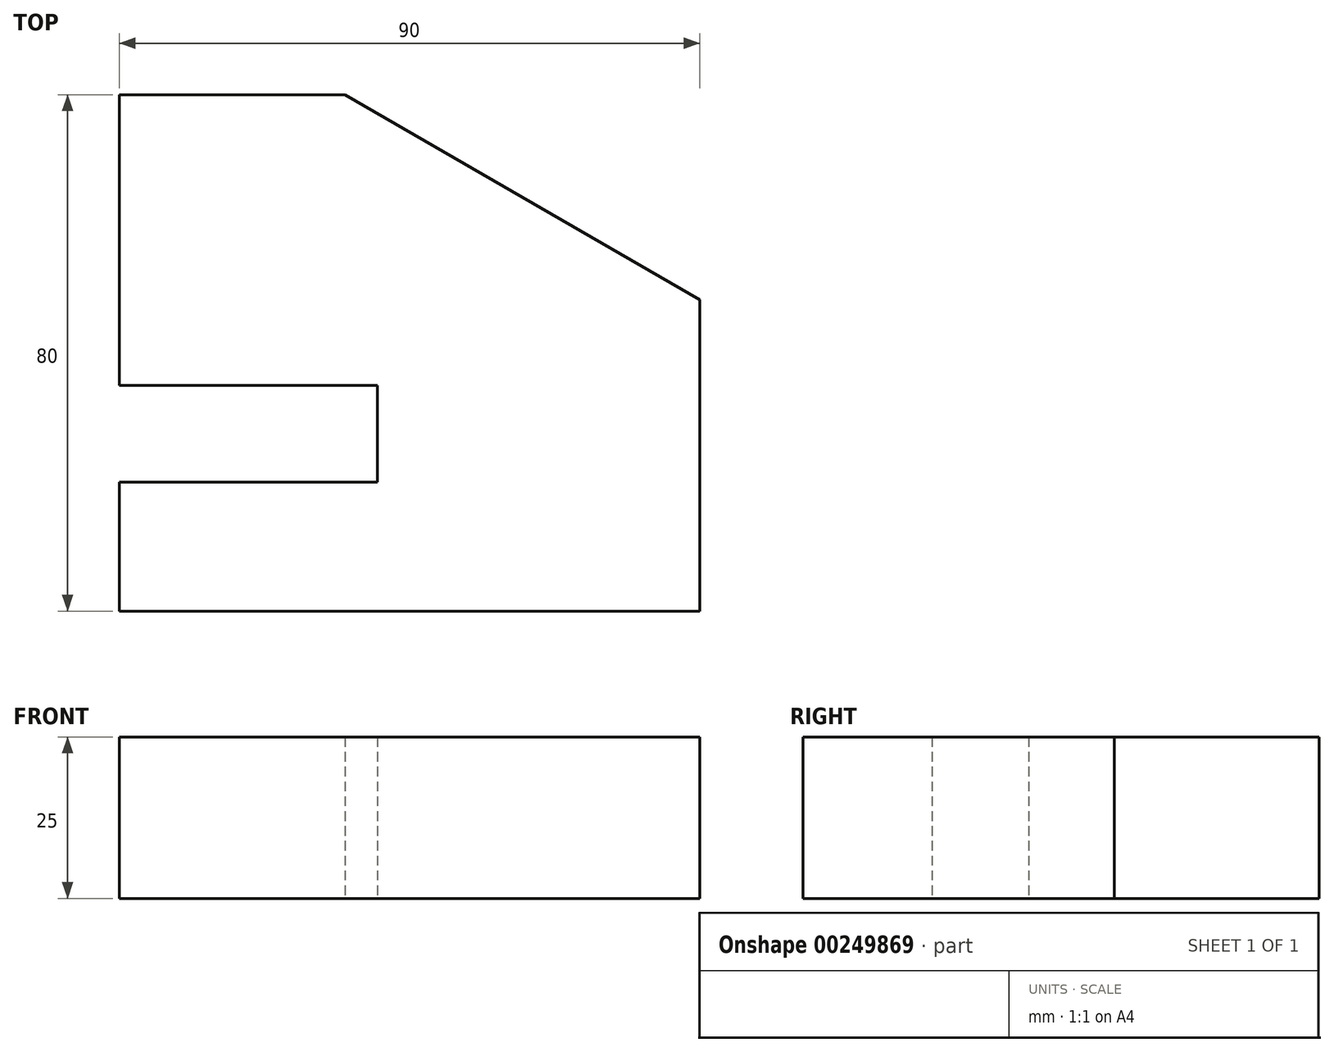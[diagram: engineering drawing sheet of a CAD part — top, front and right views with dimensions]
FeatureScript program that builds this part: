
annotation { "Feature Type Name" : "Feature", "Feature Type Description" : "" }
export const myFeature = defineFeature(function(context is Context, id is Id, definition is map)
    precondition{}
    {
        {
            var Q0;
            Q0=qCreatedBy(makeId("Top.planeOp"),FACE);
            var sketch = newSketch(context, id + "F0", { "sketchPlane" : qUnion([Q0])});
            skLineSegment(sketch, "E0", {"start": v(0, 0) * mm, "end": v(90, 0) * mm});
            skLineSegment(sketch, "E1", {"start": v(90, 0) * mm, "end": v(90, 48.25) * mm});
            skLineSegment(sketch, "E2", {"start": v(90, 48.25) * mm, "end": v(35, 80) * mm});
            skLineSegment(sketch, "E3", {"start": v(35, 80) * mm, "end": v(0, 80) * mm});
            skLineSegment(sketch, "E4", {"start": v(0, 80) * mm, "end": v(0, 35) * mm});
            skLineSegment(sketch, "E5", {"start": v(0, 35) * mm, "end": v(40, 35) * mm});
            skLineSegment(sketch, "E6", {"start": v(40, 35) * mm, "end": v(40, 20) * mm});
            skLineSegment(sketch, "E7", {"start": v(40, 20) * mm, "end": v(0, 20) * mm});
            skLineSegment(sketch, "E8", {"start": v(0, 20) * mm, "end": v(0, 0) * mm});
            skSolve(sketch);
        }
        {
            var Q0;
            Q0=makeQuery(id+"F0.imprint","IMPRINT",FACE,{"disambiguationData":[TD([[makeQuery(id+"F0.imprint","IMPRINT",EDGE,{"derivedFrom":sQuery(id+"F0.wireOp",EDGE,"E0")}),1.0]])]});
            extrude(context, id + "F1", {"entities" : qUnion([Q0]), "depth" : 25 * mm});
        }
    });
